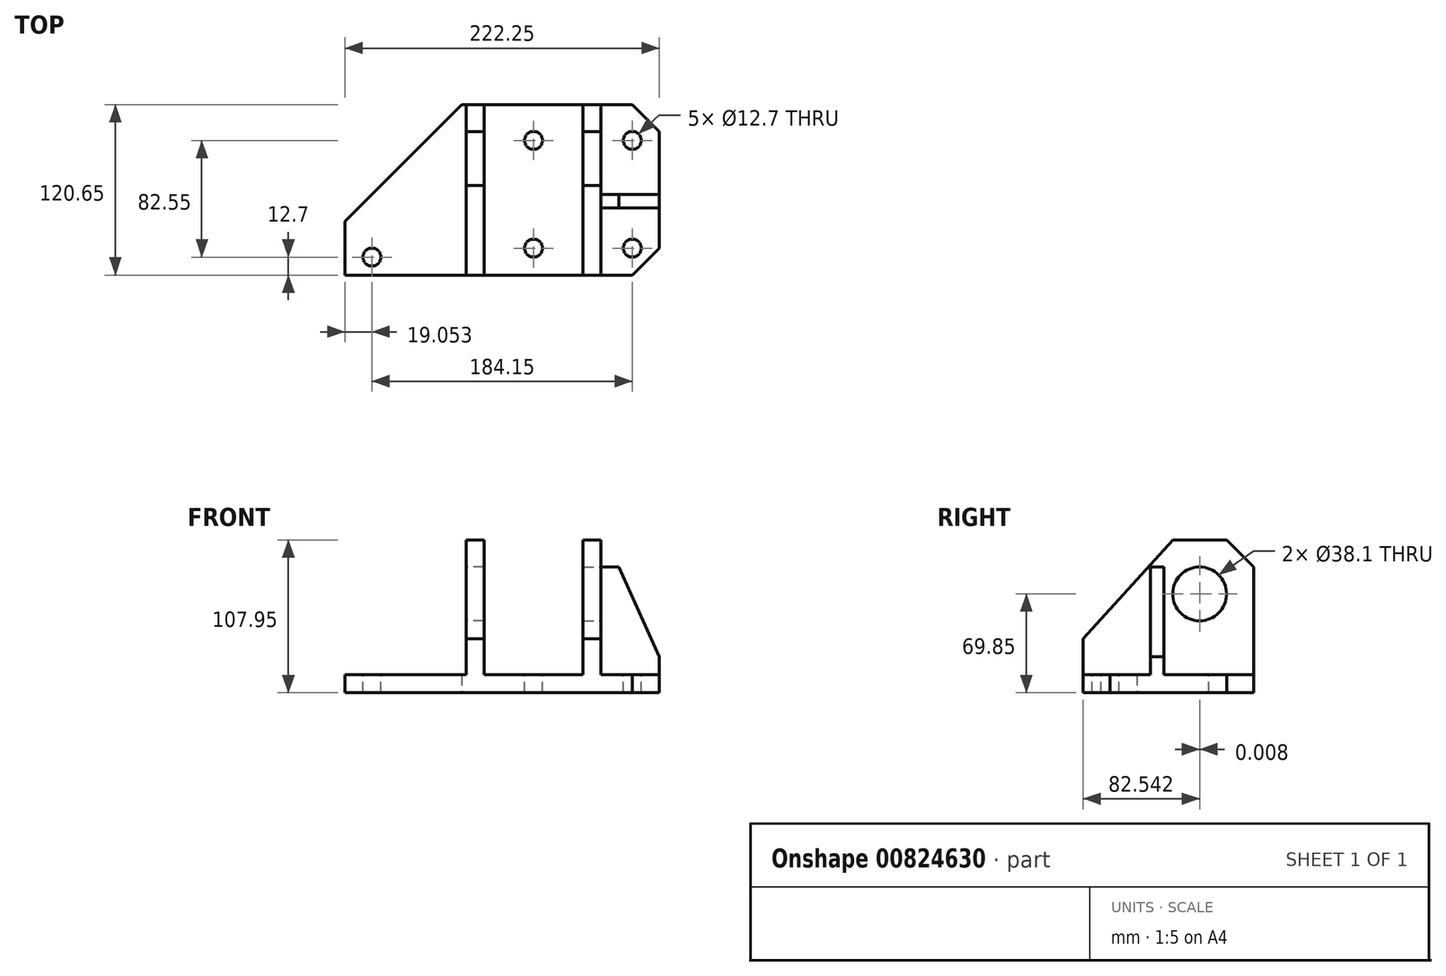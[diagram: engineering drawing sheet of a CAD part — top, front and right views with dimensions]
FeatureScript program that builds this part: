
annotation { "Feature Type Name" : "Feature", "Feature Type Description" : "" }
export const myFeature = defineFeature(function(context is Context, id is Id, definition is map)
    precondition{}
    {
        {
            var Q0;
            Q0=qCreatedBy(makeId("Top.planeOp"),FACE);
            var sketch = newSketch(context, id + "F0", { "sketchPlane" : qUnion([Q0])});
            skLineSegment(sketch, "E0", {"start": v(-62.09, -1.4) * mm, "end": v(-62.09, -39.5) * mm});
            skLineSegment(sketch, "E1", {"start": v(-62.09, -39.5) * mm, "end": v(141.11, -39.5) * mm});
            skLineSegment(sketch, "E2", {"start": v(160.16, -20.46) * mm, "end": v(160.16, 81.14) * mm});
            skLineSegment(sketch, "E3", {"start": v(160.16, -20.46) * mm, "end": v(141.11, -39.5) * mm});
            skLineSegment(sketch, "E4", {"start": v(160.16, 81.14) * mm, "end": v(71.26, 81.14) * mm});
            skLineSegment(sketch, "E5", {"start": v(71.26, 81.14) * mm, "end": v(36.34, 81.14) * mm});
            skLineSegment(sketch, "E6", {"start": v(36.34, 81.14) * mm, "end": v(20.46, 81.14) * mm});
            skLineSegment(sketch, "E7", {"start": v(20.46, 81.14) * mm, "end": v(-62.09, -1.4) * mm});
            skSolve(sketch);
        }
        {
            var Q0;
            Q0=qSketchRegion(id+"F0",true);
            extrude(context, id + "F1", {"entities" : qUnion([Q0]), "depth" : 12.7 * mm, "offsetDistance" : 25.4 * mm});
        }
        {
            var Q0;
            Q0=makeQuery(id+"F1.opExtrude","CAP_FACE",FACE,{"disambiguationData":[OSD([sQuery(id+"F0.wireOp",EDGE,"E0"),sQuery(id+"F0.wireOp",EDGE,"E1"),sQuery(id+"F0.wireOp",EDGE,"E2"),sQuery(id+"F0.wireOp",EDGE,"E3"),sQuery(id+"F0.wireOp",EDGE,"E4"),sQuery(id+"F0.wireOp",EDGE,"E5"),sQuery(id+"F0.wireOp",EDGE,"E6"),sQuery(id+"F0.wireOp",EDGE,"E7")])],"isStart":false});
            var sketch = newSketch(context, id + "F2", { "sketchPlane" : qUnion([Q0])});
            skLineSegment(sketch, "E8", {"start": v(160.16, 81.14) * mm, "end": v(160.16, 62.1) * mm});
            skLineSegment(sketch, "E9", {"start": v(160.16, 81.14) * mm, "end": v(141.11, 81.14) * mm});
            skLineSegment(sketch, "E10", {"start": v(141.11, 81.14) * mm, "end": v(160.16, 62.1) * mm});
            skSolve(sketch);
        }
        {
            var Q0;
            Q0=qSketchRegion(id+"F2",true);
            extrude(context, id + "F3", {"entities" : qUnion([Q0]), "operationType" : NewBodyOperationType.REMOVE, "oppositeDirection" : true, "depth" : 25.4 * mm, "offsetDistance" : 25.4 * mm});
        }
        {
            var Q0;
            Q0=makeQuery(id+"F1.opExtrude","CAP_FACE",FACE,{"disambiguationData":[OSD([sQuery(id+"F0.wireOp",EDGE,"E0"),sQuery(id+"F0.wireOp",EDGE,"E1"),sQuery(id+"F0.wireOp",EDGE,"E2"),sQuery(id+"F0.wireOp",EDGE,"E3"),sQuery(id+"F0.wireOp",EDGE,"E4"),sQuery(id+"F0.wireOp",EDGE,"E5"),sQuery(id+"F0.wireOp",EDGE,"E6"),sQuery(id+"F0.wireOp",EDGE,"E7")])],"isStart":false});
            var sketch = newSketch(context, id + "F4", { "sketchPlane" : qUnion([Q0])});
            skLineSegment(sketch, "E11", {"start": v(20.46, 81.14) * mm, "end": v(23.64, 81.14) * mm});
            skLineSegment(sketch, "E12", {"start": v(23.64, 81.14) * mm, "end": v(36.34, 81.14) * mm});
            skLineSegment(sketch, "E13", {"start": v(36.34, 81.14) * mm, "end": v(36.34, -39.5) * mm});
            skLineSegment(sketch, "E14", {"start": v(23.64, 81.14) * mm, "end": v(23.64, -39.5) * mm});
            skLineSegment(sketch, "E15", {"start": v(36.34, 81.14) * mm, "end": v(106.19, 81.14) * mm});
            skLineSegment(sketch, "E16", {"start": v(106.19, 81.14) * mm, "end": v(106.19, -39.5) * mm});
            skLineSegment(sketch, "E17", {"start": v(106.19, -39.5) * mm, "end": v(106.19, 81.14) * mm});
            skLineSegment(sketch, "E18", {"start": v(106.19, 81.14) * mm, "end": v(118.89, 81.14) * mm});
            skLineSegment(sketch, "E19", {"start": v(118.89, 81.14) * mm, "end": v(118.89, -39.5) * mm});
            skLineSegment(sketch, "E20", {"start": v(118.89, -39.5) * mm, "end": v(106.19, -39.5) * mm});
            skLineSegment(sketch, "E21", {"start": v(36.34, -39.5) * mm, "end": v(23.64, -39.5) * mm});
            skSolve(sketch);
        }
        {
            var Q0;
            Q0=qSketchRegion(id+"F4",true);
            extrude(context, id + "F5", {"entities" : qUnion([Q0]), "operationType" : NewBodyOperationType.ADD, "depth" : 95.25 * mm, "offsetDistance" : 25.4 * mm});
        }
        {
            var Q0;
            Q0=makeQuery(id+"F5.opExtrude","SWEPT_FACE",FACE,{"disambiguationData":[OSD([sQuery(id+"F4.wireOp",EDGE,"E14")])]});
            var sketch = newSketch(context, id + "F6", { "sketchPlane" : qUnion([Q0])});
            skLineSegment(sketch, "E22", {"start": v(-81.14, 107.95) * mm, "end": v(-62.1, 107.95) * mm});
            skLineSegment(sketch, "E23", {"start": v(-81.14, 107.95) * mm, "end": v(-81.14, 88.9) * mm});
            skLineSegment(sketch, "E24", {"start": v(-81.14, 88.9) * mm, "end": v(-62.1, 107.95) * mm});
            skSolve(sketch);
        }
        {
            var Q0;
            Q0=qSketchRegion(id+"F6",true);
            extrude(context, id + "F7", {"entities" : qUnion([Q0]), "operationType" : NewBodyOperationType.REMOVE, "oppositeDirection" : true, "depth" : 25.4 * mm, "offsetDistance" : 25.4 * mm});
        }
        {
            var Q0;
            Q0=makeQuery(id+"F5.opExtrude","SWEPT_FACE",FACE,{"disambiguationData":[OSD([sQuery(id+"F4.wireOp",EDGE,"E14")])]});
            var sketch = newSketch(context, id + "F8", { "sketchPlane" : qUnion([Q0])});
            skLineSegment(sketch, "E25", {"start": v(-62.1, 107.95) * mm, "end": v(-24, 107.95) * mm});
            skLineSegment(sketch, "E26", {"start": v(39.5, 12.7) * mm, "end": v(39.5, 38.1) * mm});
            skLineSegment(sketch, "E27", {"start": v(39.5, 38.1) * mm, "end": v(-24, 107.95) * mm});
            skSolve(sketch);
        }
        {
            var Q0;
            Q0=qSketchRegion(id+"F8",true);
            var Q1;
            {var subQ0=sQuery(id+"F8.wireOp",EDGE,"E27");Q1=makeQuery(id+"F8.imprint","IMPRINT",FACE,{"disambiguationData":[TD([[makeQuery(id+"F8.imprint","IMPRINT",EDGE,{"derivedFrom":subQ0}),-1.0]])]});}
            extrude(context, id + "F9", {"entities" : qUnion([Q0, Q1]), "operationType" : NewBodyOperationType.REMOVE, "oppositeDirection" : true, "depth" : 25.4 * mm, "offsetDistance" : 25.4 * mm});
        }
        {
            var Q0;
            Q0=makeQuery(id+"F5.opExtrude","SWEPT_FACE",FACE,{"disambiguationData":[OSD([sQuery(id+"F4.wireOp",EDGE,"E19")])]});
            var sketch = newSketch(context, id + "F10", { "sketchPlane" : qUnion([Q0])});
            skLineSegment(sketch, "E28", {"start": v(81.14, 88.9) * mm, "end": v(81.14, 107.95) * mm});
            skLineSegment(sketch, "E29", {"start": v(81.14, 107.95) * mm, "end": v(62.1, 107.95) * mm});
            skLineSegment(sketch, "E30", {"start": v(62.1, 107.95) * mm, "end": v(81.14, 88.9) * mm});
            skLineSegment(sketch, "E31", {"start": v(62.1, 107.95) * mm, "end": v(24, 107.95) * mm});
            skLineSegment(sketch, "E32", {"start": v(-39.5, 12.7) * mm, "end": v(-39.5, 38.1) * mm});
            skLineSegment(sketch, "E33", {"start": v(-39.5, 38.1) * mm, "end": v(24, 107.95) * mm});
            skSolve(sketch);
        }
        {
            var Q0;
            {var subQ0=sQuery(id+"F10.wireOp",EDGE,"E33");Q0=makeQuery(id+"F10.imprint","IMPRINT",FACE,{"disambiguationData":[TD([[makeQuery(id+"F10.imprint","IMPRINT",EDGE,{"derivedFrom":subQ0}),1.0]])]});}
            var Q1;
            Q1=makeQuery(id+"F10.imprint","IMPRINT",FACE,{"disambiguationData":[TD([[makeQuery(id+"F10.imprint","IMPRINT",EDGE,{"derivedFrom":sQuery(id+"F10.wireOp",EDGE,"E28")}),-1.0]])]});
            extrude(context, id + "F11", {"entities" : qUnion([Q0, Q1]), "operationType" : NewBodyOperationType.REMOVE, "oppositeDirection" : true, "depth" : 25.4 * mm, "offsetDistance" : 25.4 * mm});
        }
        {
            var Q0;
            {var subQ0=sQuery(id+"F0.wireOp",EDGE,"E6");var subQ1=sQuery(id+"F0.wireOp",EDGE,"E5");var subQ2=sQuery(id+"F0.wireOp",EDGE,"E4");var subQ3=sQuery(id+"F0.wireOp",EDGE,"E3");var subQ4=sQuery(id+"F0.wireOp",EDGE,"E2");var subQ5=sQuery(id+"F0.wireOp",EDGE,"E1");Q0=makeQuery(id+"F5.boolean.opBoolean","SPLIT",FACE,{"disambiguationData":[TD([makeQuery(id+"F1.opExtrude","SWEPT_FACE",FACE,{"disambiguationData":[OSD([subQ4])]})])],"derivedFrom":makeQuery(id+"F1.opExtrude","CAP_FACE",FACE,{"disambiguationData":[OSD([sQuery(id+"F0.wireOp",EDGE,"E0"),subQ5,subQ4,subQ3,subQ2,subQ1,subQ0,sQuery(id+"F0.wireOp",EDGE,"E7")])],"isStart":false})});}
            var sketch = newSketch(context, id + "F12", { "sketchPlane" : qUnion([Q0])});
            skLineSegment(sketch, "E34", {"start": v(118.89, -39.5) * mm, "end": v(118.89, 8.12) * mm});
            skLineSegment(sketch, "E35", {"start": v(118.89, 8.12) * mm, "end": v(160.16, 8.12) * mm});
            skLineSegment(sketch, "E36", {"start": v(160.16, 8.12) * mm, "end": v(160.16, 17.64) * mm});
            skLineSegment(sketch, "E37", {"start": v(160.16, 17.64) * mm, "end": v(118.89, 17.64) * mm});
            skPoint(sketch, "E37.endSnap0", {"position": v(118.89, 20.82) * mm});
            skSolve(sketch);
        }
        {
            var Q0;
            Q0=qSketchRegion(id+"F12",true);
            var Q1;
            {var subQ0=sQuery(id+"F12.wireOp",EDGE,"E35");Q1=makeQuery(id+"F12.imprint","IMPRINT",FACE,{"disambiguationData":[TD([[makeQuery(id+"F12.imprint","IMPRINT",EDGE,{"derivedFrom":subQ0}),1.0]])]});}
            extrude(context, id + "F13", {"entities" : qUnion([Q0, Q1]), "operationType" : NewBodyOperationType.ADD, "depth" : 76.2 * mm, "offsetDistance" : 25.4 * mm});
        }
        {
            var Q0;
            Q0=makeQuery(id+"F13.opExtrude","SWEPT_FACE",FACE,{"disambiguationData":[OSD([sQuery(id+"F12.wireOp",EDGE,"E35")])]});
            var sketch = newSketch(context, id + "F14", { "sketchPlane" : qUnion([Q0])});
            skLineSegment(sketch, "E38", {"start": v(118.89, 88.9) * mm, "end": v(131.59, 88.9) * mm});
            skLineSegment(sketch, "E39", {"start": v(160.16, 12.7) * mm, "end": v(160.16, 25.4) * mm});
            skLineSegment(sketch, "E40", {"start": v(160.16, 25.4) * mm, "end": v(131.59, 88.9) * mm});
            skSolve(sketch);
        }
        {
            var Q0;
            Q0=qSketchRegion(id+"F14",true);
            var Q1;
            {var subQ0=sQuery(id+"F14.wireOp",EDGE,"E40");Q1=makeQuery(id+"F14.imprint","IMPRINT",FACE,{"disambiguationData":[TD([[makeQuery(id+"F14.imprint","IMPRINT",EDGE,{"derivedFrom":subQ0}),-1.0]])]});}
            extrude(context, id + "F15", {"entities" : qUnion([Q0, Q1]), "operationType" : NewBodyOperationType.REMOVE, "oppositeDirection" : true, "depth" : 25.4 * mm, "offsetDistance" : 25.4 * mm});
        }
        {
            var Q0;
            {var subQ0=sQuery(id+"F0.wireOp",EDGE,"E7");var subQ1=sQuery(id+"F0.wireOp",EDGE,"E6");var subQ2=sQuery(id+"F0.wireOp",EDGE,"E5");var subQ3=sQuery(id+"F0.wireOp",EDGE,"E4");var subQ4=sQuery(id+"F0.wireOp",EDGE,"E1");var subQ5=sQuery(id+"F0.wireOp",EDGE,"E0");Q0=makeQuery(id+"F5.boolean.opBoolean","SPLIT",FACE,{"disambiguationData":[TD([makeQuery(id+"F1.opExtrude","SWEPT_FACE",FACE,{"disambiguationData":[OSD([subQ5])]})])],"derivedFrom":makeQuery(id+"F1.opExtrude","CAP_FACE",FACE,{"disambiguationData":[OSD([subQ5,subQ4,sQuery(id+"F0.wireOp",EDGE,"E2"),sQuery(id+"F0.wireOp",EDGE,"E3"),subQ3,subQ2,subQ1,subQ0])],"isStart":false})});}
            var sketch = newSketch(context, id + "F16", { "sketchPlane" : qUnion([Q0])});
            skLineSegment(sketch, "E41", {"start": v(-62.09, -39.5) * mm, "end": v(-43.04, -39.5) * mm});
            skLineSegment(sketch, "E42", {"start": v(-62.09, -39.5) * mm, "end": v(-62.09, -26.8) * mm});
            skLineSegment(sketch, "E43", {"start": v(-62.09, -26.8) * mm, "end": v(-43.04, -26.8) * mm});
            skCircle(sketch, "E44", {"center": v(-43.04, -26.8) * mm, "radius": 6.35 * mm});
            skSolve(sketch);
        }
        {
            var Q0;
            Q0=qSketchRegion(id+"F16",true);
            extrude(context, id + "F17", {"entities" : qUnion([Q0]), "operationType" : NewBodyOperationType.REMOVE, "oppositeDirection" : true, "depth" : 25.4 * mm, "offsetDistance" : 25.4 * mm});
        }
        {
            var Q0;
            {var subQ1=sQuery(id+"F0.wireOp",EDGE,"E2");var subQ2=makeQuery(id+"F1.opExtrude","SWEPT_FACE",FACE,{"disambiguationData":[OSD([subQ1])]});var subQ3=sQuery(id+"F0.wireOp",EDGE,"E3");var subQ6=sQuery(id+"F0.wireOp",EDGE,"E1");var subQ7=makeQuery(id+"F1.opExtrude","SWEPT_FACE",FACE,{"disambiguationData":[OSD([subQ6])]});var subQ9=sQuery(id+"F0.wireOp",EDGE,"E6");var subQ10=sQuery(id+"F0.wireOp",EDGE,"E5");var subQ11=sQuery(id+"F0.wireOp",EDGE,"E4");Q0=makeQuery(id+"F13.boolean.opBoolean","SPLIT",FACE,{"disambiguationData":[TD([subQ7])],"derivedFrom":makeQuery(id+"F5.boolean.opBoolean","SPLIT",FACE,{"disambiguationData":[TD([subQ2])],"derivedFrom":makeQuery(id+"F1.opExtrude","CAP_FACE",FACE,{"disambiguationData":[OSD([sQuery(id+"F0.wireOp",EDGE,"E0"),subQ6,subQ1,subQ3,subQ11,subQ10,subQ9,sQuery(id+"F0.wireOp",EDGE,"E7")])],"isStart":false})})});}
            var sketch = newSketch(context, id + "F18", { "sketchPlane" : qUnion([Q0])});
            skLineSegment(sketch, "E45", {"start": v(141.11, -39.5) * mm, "end": v(141.11, -20.46) * mm});
            skCircle(sketch, "E46", {"center": v(141.11, -20.46) * mm, "radius": 6.35 * mm});
            skSolve(sketch);
        }
        {
            var Q0;
            Q0=qSketchRegion(id+"F18",true);
            extrude(context, id + "F19", {"entities" : qUnion([Q0]), "operationType" : NewBodyOperationType.REMOVE, "oppositeDirection" : true, "depth" : 25.4 * mm, "offsetDistance" : 25.4 * mm});
        }
        {
            var Q0;
            {var subQ1=sQuery(id+"F0.wireOp",EDGE,"E6");var subQ2=sQuery(id+"F0.wireOp",EDGE,"E5");var subQ3=sQuery(id+"F0.wireOp",EDGE,"E4");var subQ5=makeQuery(id+"F3.boolean.opBoolean","COPY",FACE,{"derivedFrom":makeQuery(id+"F3.opExtrude","SWEPT_FACE",FACE,{"disambiguationData":[OSD([sQuery(id+"F2.wireOp",EDGE,"E10")])]})});var subQ6=sQuery(id+"F0.wireOp",EDGE,"E2");var subQ7=makeQuery(id+"F1.opExtrude","SWEPT_FACE",FACE,{"disambiguationData":[OSD([subQ6])]});var subQ10=sQuery(id+"F0.wireOp",EDGE,"E3");var subQ11=sQuery(id+"F0.wireOp",EDGE,"E1");Q0=makeQuery(id+"F13.boolean.opBoolean","SPLIT",FACE,{"disambiguationData":[TD([subQ5])],"derivedFrom":makeQuery(id+"F5.boolean.opBoolean","SPLIT",FACE,{"disambiguationData":[TD([subQ7])],"derivedFrom":makeQuery(id+"F1.opExtrude","CAP_FACE",FACE,{"disambiguationData":[OSD([sQuery(id+"F0.wireOp",EDGE,"E0"),subQ11,subQ6,subQ10,subQ3,subQ2,subQ1,sQuery(id+"F0.wireOp",EDGE,"E7")])],"isStart":false})})});}
            var sketch = newSketch(context, id + "F20", { "sketchPlane" : qUnion([Q0])});
            skLineSegment(sketch, "E47", {"start": v(141.11, 81.14) * mm, "end": v(141.11, 55.74) * mm});
            skCircle(sketch, "E48", {"center": v(141.11, 55.74) * mm, "radius": 6.35 * mm});
            skSolve(sketch);
        }
        {
            var Q0;
            Q0=makeQuery(id+"F20.imprint","IMPRINT",FACE,{"disambiguationData":[TD([[makeQuery(id+"F20.imprint","IMPRINT",EDGE,{"derivedFrom":sQuery(id+"F20.wireOp",EDGE,"E48")}),1.0]])]});
            extrude(context, id + "F21", {"entities" : qUnion([Q0]), "operationType" : NewBodyOperationType.REMOVE, "oppositeDirection" : true, "depth" : 25.4 * mm, "offsetDistance" : 25.4 * mm});
        }
        {
            var Q0;
            {var subQ0=sQuery(id+"F0.wireOp",EDGE,"E6");var subQ1=sQuery(id+"F0.wireOp",EDGE,"E5");var subQ2=sQuery(id+"F0.wireOp",EDGE,"E4");var subQ3=sQuery(id+"F0.wireOp",EDGE,"E1");Q0=makeQuery(id+"F5.boolean.opBoolean","SPLIT",FACE,{"disambiguationData":[TD([makeQuery(id+"F5.opExtrude","SWEPT_FACE",FACE,{"disambiguationData":[OSD([sQuery(id+"F4.wireOp",EDGE,"E13")])]})])],"derivedFrom":makeQuery(id+"F1.opExtrude","CAP_FACE",FACE,{"disambiguationData":[OSD([sQuery(id+"F0.wireOp",EDGE,"E0"),subQ3,sQuery(id+"F0.wireOp",EDGE,"E2"),sQuery(id+"F0.wireOp",EDGE,"E3"),subQ2,subQ1,subQ0,sQuery(id+"F0.wireOp",EDGE,"E7")])],"isStart":false})});}
            var sketch = newSketch(context, id + "F22", { "sketchPlane" : qUnion([Q0])});
            skLineSegment(sketch, "E49", {"start": v(36.34, -39.5) * mm, "end": v(71.26, -39.5) * mm});
            skLineSegment(sketch, "E50", {"start": v(71.26, -39.5) * mm, "end": v(71.26, -20.46) * mm});
            skLineSegment(sketch, "E51", {"start": v(71.26, -20.46) * mm, "end": v(71.26, 55.74) * mm});
            skCircle(sketch, "E52", {"center": v(71.26, 55.74) * mm, "radius": 6.35 * mm});
            skCircle(sketch, "E53", {"center": v(71.26, -20.46) * mm, "radius": 6.35 * mm});
            skSolve(sketch);
        }
        {
            var Q0;
            Q0=qSketchRegion(id+"F22",true);
            extrude(context, id + "F23", {"entities" : qUnion([Q0]), "operationType" : NewBodyOperationType.REMOVE, "oppositeDirection" : true, "depth" : 25.4 * mm, "offsetDistance" : 25.4 * mm});
        }
        {
            var Q0;
            Q0=makeQuery(id+"F5.opExtrude","SWEPT_FACE",FACE,{"disambiguationData":[OSD([sQuery(id+"F4.wireOp",EDGE,"E19")])]});
            var sketch = newSketch(context, id + "F24", { "sketchPlane" : qUnion([Q0])});
            skLineSegment(sketch, "E54", {"start": v(81.14, 88.9) * mm, "end": v(81.14, 69.85) * mm});
            skLineSegment(sketch, "E55", {"start": v(81.14, 69.85) * mm, "end": v(43.03, 69.85) * mm});
            skCircle(sketch, "E56", {"center": v(43.03, 69.85) * mm, "radius": 19.05 * mm});
            skSolve(sketch);
        }
        {
            var Q0;
            Q0=qSketchRegion(id+"F24",true);
            extrude(context, id + "F25", {"entities" : qUnion([Q0]), "operationType" : NewBodyOperationType.REMOVE, "oppositeDirection" : true, "depth" : 25.4 * mm, "offsetDistance" : 25.4 * mm});
        }
        {
            var Q0;
            Q0=makeQuery(id+"F5.opExtrude","SWEPT_FACE",FACE,{"disambiguationData":[OSD([sQuery(id+"F4.wireOp",EDGE,"E14")])]});
            var sketch = newSketch(context, id + "F26", { "sketchPlane" : qUnion([Q0])});
            skLineSegment(sketch, "E57", {"start": v(-81.14, 88.9) * mm, "end": v(-81.14, 69.85) * mm});
            skLineSegment(sketch, "E58", {"start": v(-81.14, 69.85) * mm, "end": v(-43.04, 69.85) * mm});
            skCircle(sketch, "E59", {"center": v(-43.04, 69.85) * mm, "radius": 19.05 * mm});
            skSolve(sketch);
        }
        {
            var Q0;
            Q0=qSketchRegion(id+"F26",true);
            extrude(context, id + "F27", {"entities" : qUnion([Q0]), "operationType" : NewBodyOperationType.REMOVE, "oppositeDirection" : true, "depth" : 25.4 * mm, "offsetDistance" : 25.4 * mm});
        }
    });
